# Revit family: 120909-00122 Шкаф ШРП-В1600-Р-ПВТ-10 ССД
name_source: partatom
category: Обобщенные модели
units: mm (PartAtom-declared; Revit-internal decimal feet)

## family parameters
Всегда вертикально = Да
Может служить основой для арматурных стержней = Нет
На основе рабочей плоскости = Нет
Общий = Нет
При загрузке вырезать с полостями = Нет
Размер круглого соединителя = Использовать диаметр
Тип детали = Нормальный
Точка расчета площади = Нет

## types (1)
- ШРП-В/1600-Р-ПВТ-10 (160 плинтов ПВТ)
    ADSK_URL документации изделия = shr_decl_2017.pdf (ssd.ru)
    ADSK_URL страницы изделия = Шкаф ШРП-В/1600-Р-ПВТ-10 ССД ( 120909-00122 ) (ssd.ru)
    ADSK_Единица измерения = шт
    ADSK_Завод-изготовитель = АО СВЯЗЬСТРОЙДЕТАЛЬ
    ADSK_Код изделия = 120909-00122
    ADSK_Масса_Текст = 99.5
    ADSK_Наименование = Шкаф ШРП-В/1600-Р-ПВТ-10 ССД
    ADSK_Наименование краткое = ШРП-В/1600-Р-ПВТ-10 (160 плинтов ПВТ)
    ADSK_Размер_Высота = 1880 мм
    ADSK_Размер_Глубина = 300 мм
    ADSK_Размер_Ширина = 860 мм
    Материал букв = Красный металл
    Материал каркаса = RAL 7035
    Ноль = 0 мм
    Описание = Шкаф ШРП-В/1600-Р-ПВТ-10 ССД
    Толшина 5 = 5 мм

## geometry (parser evidence)
native form markers: Blend x2
no freeform markers — native parametric forms only
